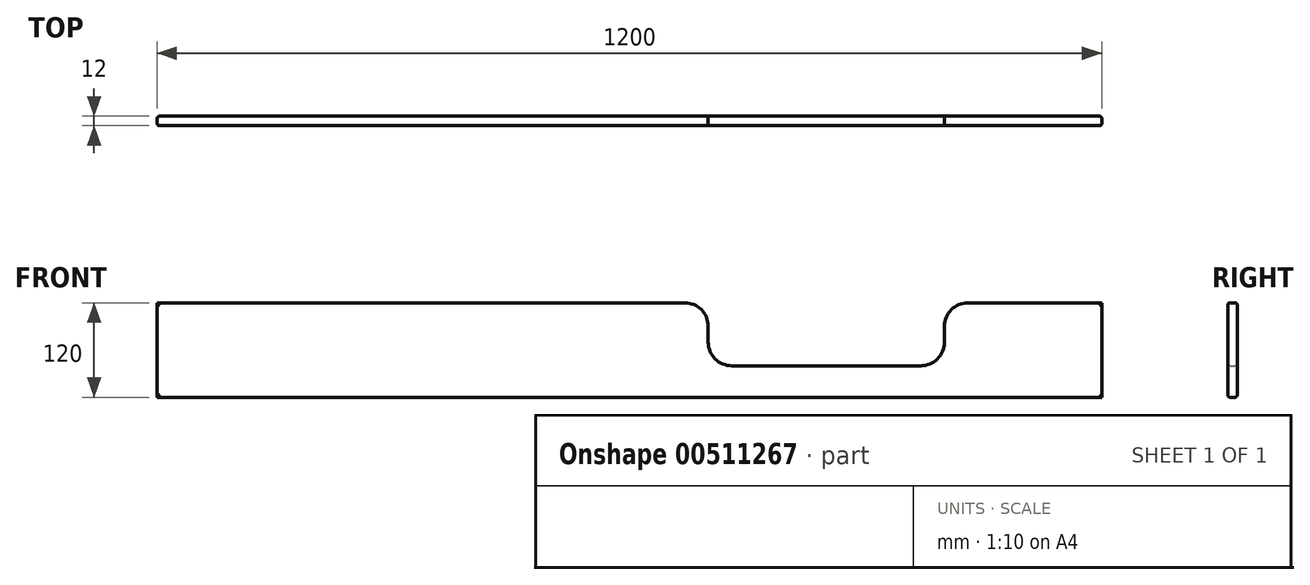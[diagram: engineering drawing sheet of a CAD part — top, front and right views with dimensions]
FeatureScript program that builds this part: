
annotation { "Feature Type Name" : "Feature", "Feature Type Description" : "" }
export const myFeature = defineFeature(function(context is Context, id is Id, definition is map)
    precondition{}
    {
        {
            var Q0;
            Q0=qCreatedBy(makeId("Front.planeOp"),FACE);
            var sketch = newSketch(context, id + "F0", { "sketchPlane" : qUnion([Q0])});
            skLineSegment(sketch, "E0.bottom", {"start": v(-521.71, 80) * mm, "end": v(148.29, 80) * mm});
            skLineSegment(sketch, "E0.top", {"start": v(-521.71, -40) * mm, "end": v(678.29, -40) * mm});
            skLineSegment(sketch, "E0.left", {"start": v(-521.71, 80) * mm, "end": v(-521.71, -40) * mm});
            skLineSegment(sketch, "E0.right", {"start": v(678.29, 80) * mm, "end": v(678.29, -40) * mm});
            skLineSegment(sketch, "E1.bottom", {"start": v(208.29, 0) * mm, "end": v(448.29, 0) * mm});
            skLineSegment(sketch, "E1.top", {"start": v(178.29, 80) * mm, "end": v(178.29, 80) * mm});
            skLineSegment(sketch, "E1.left", {"start": v(178.29, 30) * mm, "end": v(178.29, 50) * mm});
            skLineSegment(sketch, "E1.right", {"start": v(478.29, 30) * mm, "end": v(478.29, 50) * mm});
            skLineSegment(sketch, "E2", {"start": v(478.29, 80) * mm, "end": v(478.29, 80) * mm});
            skLineSegment(sketch, "E3", {"start": v(508.29, 80) * mm, "end": v(678.29, 80) * mm});
            skPoint(sketch, "E4.visualSharp", {"position": v(178.29, 0) * mm});
            skArc(sketch, "E4.filletArc", {"start": v(178.29, 30) * mm, "mid": v(187.07, 8.79) * mm, "end": v(208.29, 0) * mm});
            skPoint(sketch, "E5.visualSharp", {"position": v(478.29, 0) * mm});
            skArc(sketch, "E5.filletArc", {"start": v(448.29, 0) * mm, "mid": v(469.5, 8.79) * mm, "end": v(478.29, 30) * mm});
            skPoint(sketch, "E6.visualSharp", {"position": v(178.29, 80) * mm});
            skArc(sketch, "E6.filletArc", {"start": v(178.29, 50) * mm, "mid": v(169.5, 71.21) * mm, "end": v(148.29, 80) * mm});
            skPoint(sketch, "E7.visualSharp", {"position": v(478.29, 80) * mm});
            skArc(sketch, "E7.filletArc", {"start": v(508.29, 80) * mm, "mid": v(487.07, 71.21) * mm, "end": v(478.29, 50) * mm});
            skSolve(sketch);
        }
        {
            var Q0;
            Q0=makeQuery(id+"F0.imprint","IMPRINT",FACE,{"disambiguationData":[TD([[makeQuery(id+"F0.imprint","IMPRINT",EDGE,{"derivedFrom":sQuery(id+"F0.wireOp",EDGE,"E0.bottom")}),-1.0]])]});
            extrude(context, id + "F1", {"entities" : qUnion([Q0]), "depth" : 12 * mm});
        }
        {
            var Q0;
            Q0=makeQuery(id+"F1.opExtrude","CAP_FACE",FACE,{"disambiguationData":[OSD([sQuery(id+"F0.wireOp",EDGE,"E0.bottom"),sQuery(id+"F0.wireOp",EDGE,"E0.top"),sQuery(id+"F0.wireOp",EDGE,"E0.left"),sQuery(id+"F0.wireOp",EDGE,"E0.right"),sQuery(id+"F0.wireOp",EDGE,"E1.bottom"),sQuery(id+"F0.wireOp",EDGE,"E1.left"),sQuery(id+"F0.wireOp",EDGE,"E1.right"),sQuery(id+"F0.wireOp",EDGE,"E3"),sQuery(id+"F0.wireOp",EDGE,"E4.filletArc"),sQuery(id+"F0.wireOp",EDGE,"E5.filletArc"),sQuery(id+"F0.wireOp",EDGE,"E6.filletArc"),sQuery(id+"F0.wireOp",EDGE,"E7.filletArc")])],"isStart":true});
            var sketch = newSketch(context, id + "F2", { "sketchPlane" : qUnion([Q0])});
            skLineSegment(sketch, "E8", {"start": v(521.71, -40) * mm, "end": v(521.71, -20) * mm});
            skLineSegment(sketch, "E9", {"start": v(521.71, -20) * mm, "end": v(-678.29, -20) * mm});
            skPoint(sketch, "E10", {"position": v(-78.29, -20) * mm});
            skLineSegment(sketch, "E11", {"start": v(-678.29, -40) * mm, "end": v(-678.29, -6) * mm});
            skLineSegment(sketch, "E12", {"start": v(-678.29, -6) * mm, "end": v(521.71, -6) * mm});
            skPoint(sketch, "E13", {"position": v(-78.29, -6) * mm});
            skSolve(sketch);
        }
        {
            var Q0;
            Q0=makeQuery(id+"F1.opExtrude","CAP_FACE",FACE,{"disambiguationData":[OSD([sQuery(id+"F0.wireOp",EDGE,"E0.bottom"),sQuery(id+"F0.wireOp",EDGE,"E0.top"),sQuery(id+"F0.wireOp",EDGE,"E0.left"),sQuery(id+"F0.wireOp",EDGE,"E0.right"),sQuery(id+"F0.wireOp",EDGE,"E1.bottom"),sQuery(id+"F0.wireOp",EDGE,"E1.left"),sQuery(id+"F0.wireOp",EDGE,"E1.right"),sQuery(id+"F0.wireOp",EDGE,"E3"),sQuery(id+"F0.wireOp",EDGE,"E4.filletArc"),sQuery(id+"F0.wireOp",EDGE,"E5.filletArc"),sQuery(id+"F0.wireOp",EDGE,"E6.filletArc"),sQuery(id+"F0.wireOp",EDGE,"E7.filletArc")])],"isStart":true});
            var Q1;
            Q1=makeQuery(id+"F1.opExtrude","CAP_FACE",FACE,{"disambiguationData":[OSD([sQuery(id+"F0.wireOp",EDGE,"E0.bottom"),sQuery(id+"F0.wireOp",EDGE,"E0.top"),sQuery(id+"F0.wireOp",EDGE,"E0.left"),sQuery(id+"F0.wireOp",EDGE,"E0.right"),sQuery(id+"F0.wireOp",EDGE,"E1.bottom"),sQuery(id+"F0.wireOp",EDGE,"E1.left"),sQuery(id+"F0.wireOp",EDGE,"E1.right"),sQuery(id+"F0.wireOp",EDGE,"E3"),sQuery(id+"F0.wireOp",EDGE,"E4.filletArc"),sQuery(id+"F0.wireOp",EDGE,"E5.filletArc"),sQuery(id+"F0.wireOp",EDGE,"E6.filletArc"),sQuery(id+"F0.wireOp",EDGE,"E7.filletArc")])],"isStart":false});
            fillet(context, id + "F3", {"entities" : qUnion([Q0, Q1]), "radius" : 3 * mm, "tangentPropagation" : true, "allowEdgeOverflow" : false});
        }
    });
